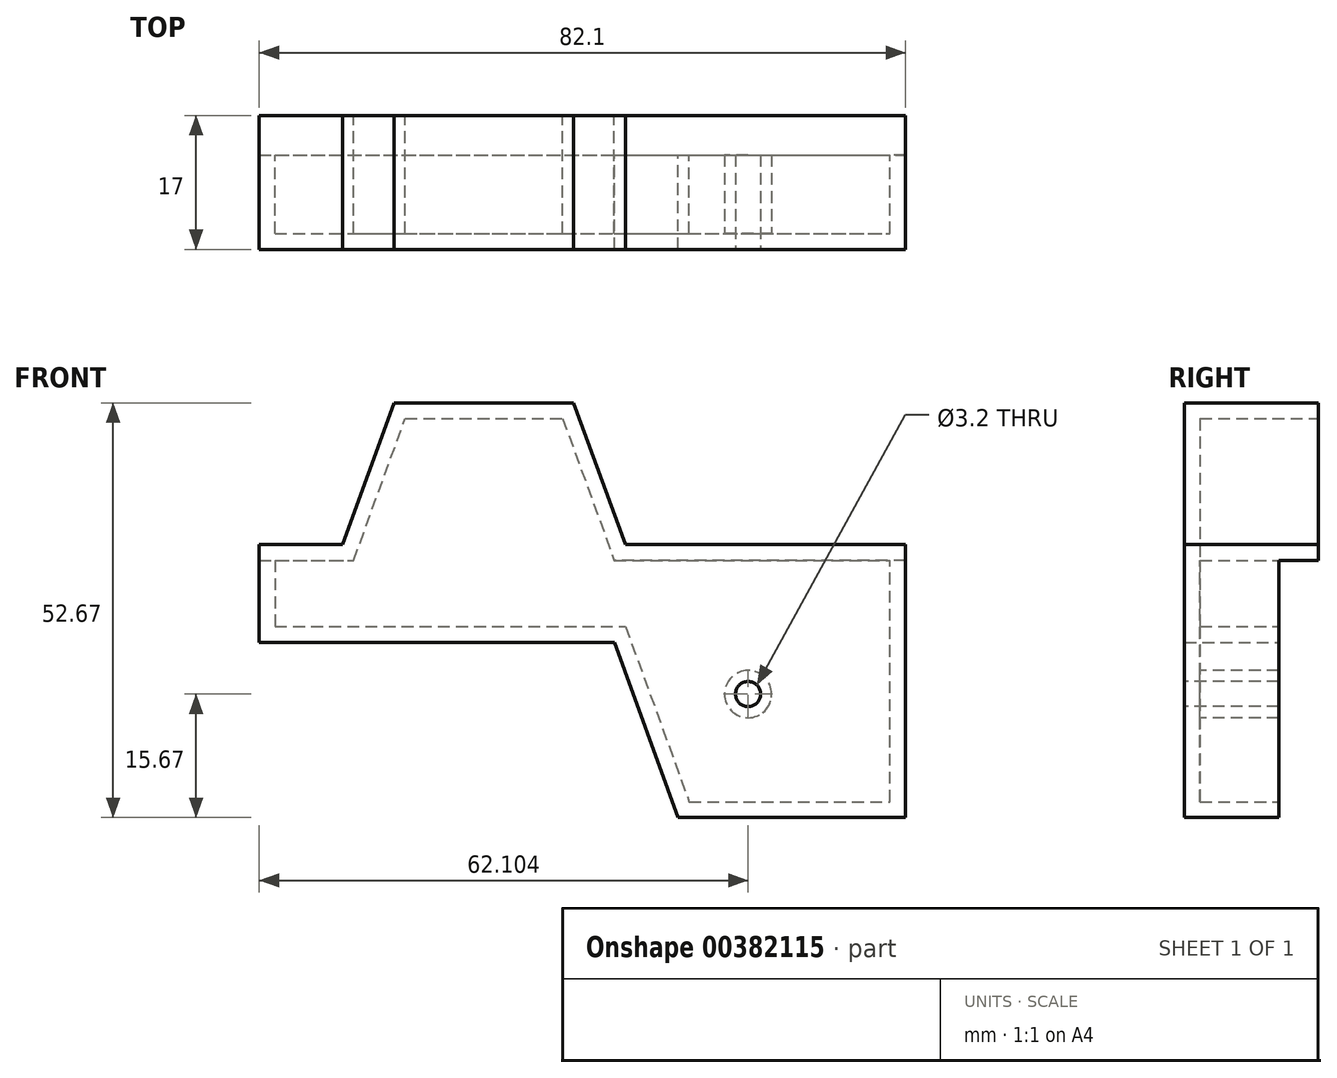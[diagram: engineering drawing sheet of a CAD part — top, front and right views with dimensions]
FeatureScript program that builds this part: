
annotation { "Feature Type Name" : "Feature", "Feature Type Description" : "" }
export const myFeature = defineFeature(function(context is Context, id is Id, definition is map)
    precondition{}
    {
        {
            var Q0;
            Q0=qCreatedBy(makeId("Front.planeOp"),FACE);
            var sketch = newSketch(context, id + "F0", { "sketchPlane" : qUnion([Q0])});
            skLineSegment(sketch, "E0", {"start": v(-23.96, 0) * mm, "end": v(-13.96, 0) * mm});
            skLineSegment(sketch, "E1", {"start": v(-13.96, 0) * mm, "end": v(-7.4, 18) * mm});
            skLineSegment(sketch, "E2", {"start": v(-7.4, 18) * mm, "end": v(12.6, 18) * mm});
            skLineSegment(sketch, "E3", {"start": v(12.6, 18) * mm, "end": v(19.14, 0) * mm});
            skLineSegment(sketch, "E4", {"start": v(19.14, 0) * mm, "end": v(54.14, 0) * mm});
            skLineSegment(sketch, "E5", {"start": v(54.14, 2) * mm, "end": v(54.14, 0) * mm});
            skLineSegment(sketch, "E6", {"start": v(-23.96, 0) * mm, "end": v(-23.96, -8.42) * mm});
            skLineSegment(sketch, "E7", {"start": v(-23.96, -8.42) * mm, "end": v(20.57, -8.42) * mm});
            skLineSegment(sketch, "E8", {"start": v(20.57, -8.42) * mm, "end": v(28.67, -30.67) * mm});
            skLineSegment(sketch, "E9", {"start": v(28.67, -30.67) * mm, "end": v(54.14, -30.67) * mm});
            skLineSegment(sketch, "E10", {"start": v(54.14, -30.67) * mm, "end": v(54.14, 0) * mm});
            skSolve(sketch);
        }
        {
            var Q0;
            Q0 = qSketchRegion(id + "F0", true);
            extrude(context, id + "F1", {"entities" : qUnion([Q0]), "depth" : 10 * mm});
        }
        {
            var Q0;
            Q0=makeQuery(id+"F1.opExtrude","CAP_FACE",FACE,{"disambiguationData":[OSD([sQuery(id+"F0.wireOp",EDGE,"E0"),sQuery(id+"F0.wireOp",EDGE,"E1"),sQuery(id+"F0.wireOp",EDGE,"E2"),sQuery(id+"F0.wireOp",EDGE,"E3"),sQuery(id+"F0.wireOp",EDGE,"E4"),sQuery(id+"F0.wireOp",EDGE,"E6"),sQuery(id+"F0.wireOp",EDGE,"E7"),sQuery(id+"F0.wireOp",EDGE,"E8"),sQuery(id+"F0.wireOp",EDGE,"E9"),sQuery(id+"F0.wireOp",EDGE,"E10")])],"isStart":true});
            shell(context, id + "F2", {"entities" : qUnion([Q0]), "thickness" : 2 * mm, "oppositeDirection" : true});
        }
        {
            var Q0;
            Q0=makeQuery(id+"F1.opExtrude","CAP_FACE",FACE,{"disambiguationData":[OSD([sQuery(id+"F0.wireOp",EDGE,"E0"),sQuery(id+"F0.wireOp",EDGE,"E1"),sQuery(id+"F0.wireOp",EDGE,"E2"),sQuery(id+"F0.wireOp",EDGE,"E3"),sQuery(id+"F0.wireOp",EDGE,"E4"),sQuery(id+"F0.wireOp",EDGE,"E6"),sQuery(id+"F0.wireOp",EDGE,"E7"),sQuery(id+"F0.wireOp",EDGE,"E8"),sQuery(id+"F0.wireOp",EDGE,"E9"),sQuery(id+"F0.wireOp",EDGE,"E10")])],"isStart":true});
            var sketch = newSketch(context, id + "F3", { "sketchPlane" : qUnion([Q0])});
            skLineSegment(sketch, "E11", {"start": v(-54.14, 0) * mm, "end": v(-19.14, 0) * mm});
            skLineSegment(sketch, "E12", {"start": v(-19.14, 0) * mm, "end": v(-12.6, 18) * mm});
            skLineSegment(sketch, "E13", {"start": v(-12.6, 18) * mm, "end": v(7.4, 18) * mm});
            skLineSegment(sketch, "E14", {"start": v(7.4, 18) * mm, "end": v(13.96, 0) * mm});
            skLineSegment(sketch, "E15", {"start": v(13.96, 0) * mm, "end": v(25.96, 0) * mm});
            skLineSegment(sketch, "E16", {"start": v(25.96, 0) * mm, "end": v(25.96, 2) * mm});
            skLineSegment(sketch, "E17", {"start": v(25.96, 2) * mm, "end": v(15.36, 2) * mm});
            skLineSegment(sketch, "E18", {"start": v(15.36, 2) * mm, "end": v(8.8, 20) * mm});
            skLineSegment(sketch, "E19", {"start": v(8.8, 20) * mm, "end": v(-14, 20) * mm});
            skLineSegment(sketch, "E20", {"start": v(-14, 20) * mm, "end": v(-20.54, 2) * mm});
            skLineSegment(sketch, "E21", {"start": v(-20.54, 2) * mm, "end": v(-56.14, 2) * mm});
            skLineSegment(sketch, "E22", {"start": v(-56.14, 2) * mm, "end": v(-56.14, 0) * mm});
            skLineSegment(sketch, "E23", {"start": v(-56.14, 0) * mm, "end": v(-54.14, 0) * mm});
            skSolve(sketch);
        }
        {
            var Q0;
            Q0 = qSketchRegion(id + "F3", true);
            extrude(context, id + "F4", {"entities" : qUnion([Q0]), "operationType" : NewBodyOperationType.ADD, "depth" : 5 * mm});
        }
        {
            var Q0;
            Q0=makeQuery(id+"F2.opShell","OFFSET_FACE",FACE,{"disambiguationData":[OSD([sQuery(id+"F0.wireOp",EDGE,"E0"),sQuery(id+"F0.wireOp",EDGE,"E1"),sQuery(id+"F0.wireOp",EDGE,"E2"),sQuery(id+"F0.wireOp",EDGE,"E3"),sQuery(id+"F0.wireOp",EDGE,"E4"),sQuery(id+"F0.wireOp",EDGE,"E6"),sQuery(id+"F0.wireOp",EDGE,"E7"),sQuery(id+"F0.wireOp",EDGE,"E8"),sQuery(id+"F0.wireOp",EDGE,"E9"),sQuery(id+"F0.wireOp",EDGE,"E10")])]});
            var sketch = newSketch(context, id + "F5", { "sketchPlane" : qUnion([Q0])});
            skCircle(sketch, "E24", {"center": v(-36.14, -17) * mm, "radius": 1.6 * mm});
            skCircle(sketch, "E25", {"center": v(-36.14, -17) * mm, "radius": 3 * mm});
            skSolve(sketch);
        }
        {
            var Q0;
            Q0 = qSketchRegion(id + "F5", true);
            var Q1;
            {var subQ0=sQuery(id+"F0.wireOp",EDGE,"E9");var subQ1=sQuery(id+"F0.wireOp",EDGE,"E8");Q1=makeQuery(id+"F2.opShell","OFFSET_VERTEX",VERTEX,{"disambiguationData":[OSD([subQ1,subQ0]),TDD([makeQuery(id+"F1.opExtrude","CAP_VERTEX",VERTEX,{"disambiguationData":[OSD([subQ1,subQ0])],"isStart":true})])]});}
            extrude(context, id + "F6", {"entities" : qUnion([Q0]), "operationType" : NewBodyOperationType.ADD, "endBound" : BoundingType.UP_TO_VERTEX, "endBoundEntityVertex" : qUnion([Q1]), "depth" : 25 * mm});
        }
        {
            var Q0;
            Q0=makeQuery(id+"F6.boolean.opBoolean","SPLIT",FACE,{"disambiguationData":[TD([makeQuery(id+"F6.opExtrude","SWEPT_FACE",FACE,{"disambiguationData":[OSD([sQuery(id+"F5.wireOp",EDGE,"E24")])]})])],"derivedFrom":makeQuery(id+"F2.opShell","OFFSET_FACE",FACE,{"disambiguationData":[OSD([sQuery(id+"F0.wireOp",EDGE,"E0"),sQuery(id+"F0.wireOp",EDGE,"E1"),sQuery(id+"F0.wireOp",EDGE,"E2"),sQuery(id+"F0.wireOp",EDGE,"E3"),sQuery(id+"F0.wireOp",EDGE,"E4"),sQuery(id+"F0.wireOp",EDGE,"E6"),sQuery(id+"F0.wireOp",EDGE,"E7"),sQuery(id+"F0.wireOp",EDGE,"E8"),sQuery(id+"F0.wireOp",EDGE,"E9"),sQuery(id+"F0.wireOp",EDGE,"E10")])]})});
            extrude(context, id + "F7", {"entities" : qUnion([Q0]), "operationType" : NewBodyOperationType.REMOVE, "endBound" : BoundingType.THROUGH_ALL, "oppositeDirection" : true, "depth" : 25 * mm});
        }
    });
